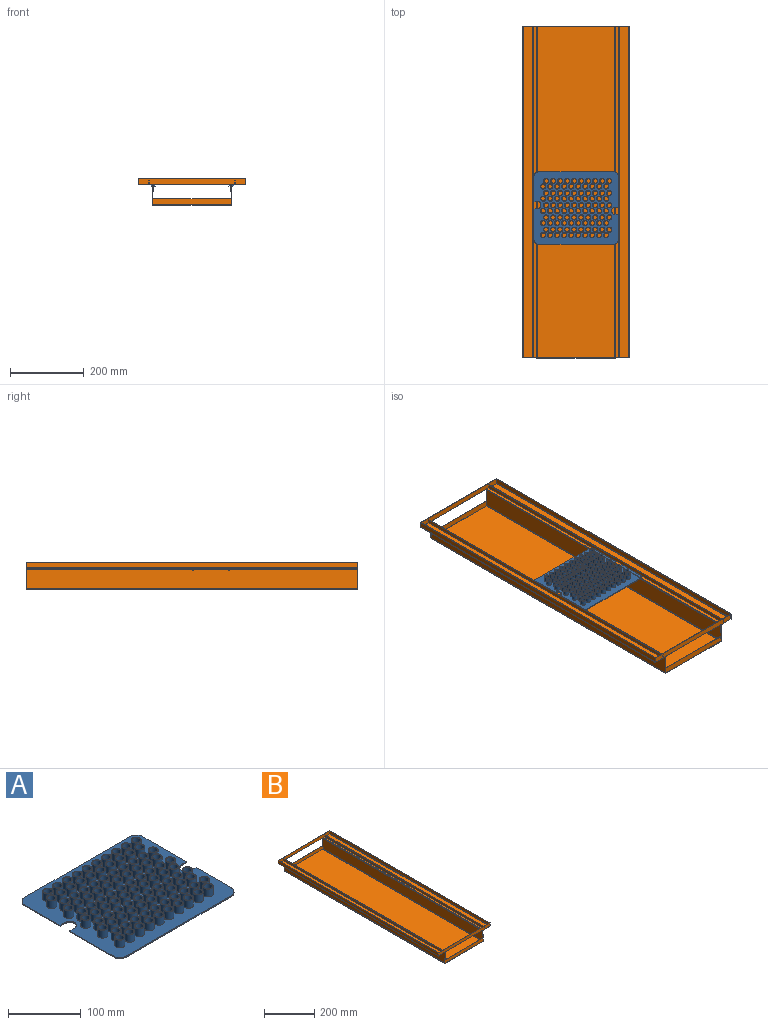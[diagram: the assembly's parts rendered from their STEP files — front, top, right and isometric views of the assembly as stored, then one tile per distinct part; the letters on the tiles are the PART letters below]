
ASSEMBLY  parts=2 mates=1
PART A: 338 faces, bbox 229x197x19 mm
  f0: plane 203x2mm, normal (0,1,0), area 406mm2, adj f1,f115,f116,f117
  f1: cylinder r=13mm len=13mm, axis (0,0,-1), area 37.4mm2, adj f0,f2,f116,f117,f136
  f2: plane 68x1mm, normal (-1,0,0), area 68mm2, adj f1,f3,f116,f136
  f3: plane 9.5x2mm, normal (0,-1,0), area 18.5mm2, adj f2,f4,f116,f117,f136
  f4: cylinder r=9.5mm len=19mm, axis (0,0,-1), area 59.7mm2, adj f3,f5,f116,f117
  f5: plane 9.5x2mm, normal (0,1,0), area 18.5mm2, adj f4,f6,f116,f117,f137
  f6: plane 84x1mm, normal (-1,0,0), area 84mm2, adj f5,f7,f116,f137
  f7: cylinder r=13mm len=13mm, axis (0,0,-1), area 37.4mm2, adj f6,f8,f116,f117,f137
  f8: plane 203x2mm, normal (0,-1,0), area 406mm2, adj f7,f9,f116,f117
  f9: cylinder r=13mm len=13mm, axis (0,0,-1), area 37.4mm2, adj f8,f10,f116,f117,f135
  f10: plane 68x1mm, normal (1,0,0), area 68mm2, adj f9,f11,f116,f135
  f11: plane 9.5x2mm, normal (0,1,0), area 18.5mm2, adj f10,f12,f116,f117,f135
  f12: cylinder r=9.5mm len=19mm, axis (0,0,-1), area 59.7mm2, adj f11,f13,f116,f117
  f13: plane 9.5x2mm, normal (0,-1,0), area 18.5mm2, adj f12,f14,f116,f117,f134
  f14: plane 84x1mm, normal (1,0,0), area 84mm2, adj f13,f115,f116,f134
  f15: cylinder r=6mm len=15mm, axis (0,0,-1), area 565.5mm2, adj f117,f229
  f16: cylinder r=6mm len=15mm, axis (0,0,-1), area 565.5mm2, adj f117,f337
  f17: cylinder r=6mm len=15mm, axis (0,0,-1), area 565.5mm2, adj f117,f231
  f18: cylinder r=6mm len=15mm, axis (0,0,-1), area 565.5mm2, adj f117,f233
  f19: cylinder r=6mm len=15mm, axis (0,0,-1), area 565.5mm2, adj f117,f235
  f20: cylinder r=6mm len=15mm, axis (0,0,-1), area 565.5mm2, adj f117,f237
  f21: cylinder r=6mm len=15mm, axis (0,0,-1), area 565.5mm2, adj f117,f219
  f22: cylinder r=6mm len=15mm, axis (0,0,-1), area 565.5mm2, adj f117,f221
  f23: cylinder r=6mm len=15mm, axis (0,0,-1), area 565.5mm2, adj f117,f223
  f24: cylinder r=6mm len=15mm, axis (0,0,-1), area 565.5mm2, adj f117,f225
  f25: cylinder r=6mm len=15mm, axis (0,0,-1), area 565.5mm2, adj f117,f227
  f26: cylinder r=6mm len=15mm, axis (0,0,-1), area 565.5mm2, adj f117,f209
  f27: cylinder r=6mm len=15mm, axis (0,0,-1), area 565.5mm2, adj f117,f211
  f28: cylinder r=6mm len=15mm, axis (0,0,-1), area 565.5mm2, adj f117,f213
  f29: cylinder r=6mm len=15mm, axis (0,0,-1), area 565.5mm2, adj f117,f215
  f30: cylinder r=6mm len=15mm, axis (0,0,-1), area 565.5mm2, adj f117,f217
  f31: cylinder r=6mm len=15mm, axis (0,0,-1), area 565.5mm2, adj f117,f199
  f32: cylinder r=6mm len=15mm, axis (0,0,-1), area 565.5mm2, adj f117,f201
  f33: cylinder r=6mm len=15mm, axis (0,0,-1), area 565.5mm2, adj f117,f203
  f34: cylinder r=6mm len=15mm, axis (0,0,-1), area 565.5mm2, adj f117,f205
  f35: cylinder r=6mm len=15mm, axis (0,0,-1), area 565.5mm2, adj f117,f207
  f36: cylinder r=6mm len=15mm, axis (0,0,-1), area 565.5mm2, adj f117,f189
  f37: cylinder r=6mm len=15mm, axis (0,0,-1), area 565.5mm2, adj f117,f191
  f38: cylinder r=6mm len=15mm, axis (0,0,-1), area 565.5mm2, adj f117,f193
  f39: cylinder r=6mm len=15mm, axis (0,0,-1), area 565.5mm2, adj f117,f195
  f40: cylinder r=6mm len=15mm, axis (0,0,-1), area 565.5mm2, adj f117,f197
  f41: cylinder r=6mm len=15mm, axis (0,0,-1), area 565.5mm2, adj f117,f179
  f42: cylinder r=6mm len=15mm, axis (0,0,-1), area 565.5mm2, adj f117,f181
  f43: cylinder r=6mm len=15mm, axis (0,0,-1), area 565.5mm2, adj f117,f183
  f44: cylinder r=6mm len=15mm, axis (0,0,-1), area 565.5mm2, adj f117,f185
  f45: cylinder r=6mm len=15mm, axis (0,0,-1), area 565.5mm2, adj f117,f187
  f46: cylinder r=6mm len=15mm, axis (0,0,-1), area 565.5mm2, adj f117,f169
  f47: cylinder r=6mm len=15mm, axis (0,0,-1), area 565.5mm2, adj f117,f171
  f48: cylinder r=6mm len=15mm, axis (0,0,-1), area 565.5mm2, adj f117,f173
  f49: cylinder r=6mm len=15mm, axis (0,0,-1), area 565.5mm2, adj f117,f175
  f50: cylinder r=6mm len=15mm, axis (0,0,-1), area 565.5mm2, adj f117,f177
  f51: cylinder r=6mm len=15mm, axis (0,0,-1), area 565.5mm2, adj f117,f159
  f52: cylinder r=6mm len=15mm, axis (0,0,-1), area 565.5mm2, adj f117,f161
  f53: cylinder r=6mm len=15mm, axis (0,0,-1), area 565.5mm2, adj f117,f163
  f54: cylinder r=6mm len=15mm, axis (0,0,-1), area 565.5mm2, adj f117,f165
  f55: cylinder r=6mm len=15mm, axis (0,0,-1), area 565.5mm2, adj f117,f167
  f56: cylinder r=6mm len=15mm, axis (0,0,-1), area 565.5mm2, adj f117,f149
  f57: cylinder r=6mm len=15mm, axis (0,0,-1), area 565.5mm2, adj f117,f151
  f58: cylinder r=6mm len=15mm, axis (0,0,-1), area 565.5mm2, adj f117,f153
  f59: cylinder r=6mm len=15mm, axis (0,0,-1), area 565.5mm2, adj f117,f155
  f60: cylinder r=6mm len=15mm, axis (0,0,-1), area 565.5mm2, adj f117,f157
  f61: cylinder r=6mm len=15mm, axis (0,0,-1), area 565.5mm2, adj f117,f139
  f62: cylinder r=6mm len=15mm, axis (0,0,-1), area 565.5mm2, adj f117,f141
  f63: cylinder r=6mm len=15mm, axis (0,0,-1), area 565.5mm2, adj f117,f143
  f64: cylinder r=6mm len=15mm, axis (0,0,-1), area 565.5mm2, adj f117,f145
  f65: cylinder r=6mm len=15mm, axis (0,0,-1), area 565.5mm2, adj f117,f147
  f66: cylinder r=6mm len=15mm, axis (0,0,-1), area 565.5mm2, adj f117,f335
  f67: cylinder r=6mm len=15mm, axis (0,0,-1), area 565.5mm2, adj f117,f333
  f68: cylinder r=6mm len=15mm, axis (0,0,-1), area 565.5mm2, adj f117,f331
  f69: cylinder r=6mm len=15mm, axis (0,0,-1), area 565.5mm2, adj f117,f329
  f70: cylinder r=6mm len=15mm, axis (0,0,-1), area 565.5mm2, adj f117,f327
  f71: cylinder r=6mm len=15mm, axis (0,0,-1), area 565.5mm2, adj f117,f325
  f72: cylinder r=6mm len=15mm, axis (0,0,-1), area 565.5mm2, adj f117,f323
  f73: cylinder r=6mm len=15mm, axis (0,0,-1), area 565.5mm2, adj f117,f321
  f74: cylinder r=6mm len=15mm, axis (0,0,-1), area 565.5mm2, adj f117,f319
  f75: cylinder r=6mm len=15mm, axis (0,0,-1), area 565.5mm2, adj f117,f317
  f76: cylinder r=6mm len=15mm, axis (0,0,-1), area 565.5mm2, adj f117,f315
  f77: cylinder r=6mm len=15mm, axis (0,0,-1), area 565.5mm2, adj f117,f313
  f78: cylinder r=6mm len=15mm, axis (0,0,-1), area 565.5mm2, adj f117,f311
  f79: cylinder r=6mm len=15mm, axis (0,0,-1), area 565.5mm2, adj f117,f309
  f80: cylinder r=6mm len=15mm, axis (0,0,-1), area 565.5mm2, adj f117,f307
  f81: cylinder r=6mm len=15mm, axis (0,0,-1), area 565.5mm2, adj f117,f305
  f82: cylinder r=6mm len=15mm, axis (0,0,-1), area 565.5mm2, adj f117,f303
  f83: cylinder r=6mm len=15mm, axis (0,0,-1), area 565.5mm2, adj f117,f301
  f84: cylinder r=6mm len=15mm, axis (0,0,-1), area 565.5mm2, adj f117,f299
  f85: cylinder r=6mm len=15mm, axis (0,0,-1), area 565.5mm2, adj f117,f297
  f86: cylinder r=6mm len=15mm, axis (0,0,-1), area 565.5mm2, adj f117,f295
  f87: cylinder r=6mm len=15mm, axis (0,0,-1), area 565.5mm2, adj f117,f293
  f88: cylinder r=6mm len=15mm, axis (0,0,-1), area 565.5mm2, adj f117,f291
  f89: cylinder r=6mm len=15mm, axis (0,0,-1), area 565.5mm2, adj f117,f289
  f90: cylinder r=6mm len=15mm, axis (0,0,-1), area 565.5mm2, adj f117,f287
  f91: cylinder r=6mm len=15mm, axis (0,0,-1), area 565.5mm2, adj f117,f285
  f92: cylinder r=6mm len=15mm, axis (0,0,-1), area 565.5mm2, adj f117,f283
  f93: cylinder r=6mm len=15mm, axis (0,0,-1), area 565.5mm2, adj f117,f281
  f94: cylinder r=6mm len=15mm, axis (0,0,-1), area 565.5mm2, adj f117,f279
  f95: cylinder r=6mm len=15mm, axis (0,0,-1), area 565.5mm2, adj f117,f277
  f96: cylinder r=6mm len=15mm, axis (0,0,-1), area 565.5mm2, adj f117,f275
  f97: cylinder r=6mm len=15mm, axis (0,0,-1), area 565.5mm2, adj f117,f273
  f98: cylinder r=6mm len=15mm, axis (0,0,-1), area 565.5mm2, adj f117,f271
  f99: cylinder r=6mm len=15mm, axis (0,0,-1), area 565.5mm2, adj f117,f269
  f100: cylinder r=6mm len=15mm, axis (0,0,-1), area 565.5mm2, adj f117,f267
  f101: cylinder r=6mm len=15mm, axis (0,0,-1), area 565.5mm2, adj f117,f265
  f102: cylinder r=6mm len=15mm, axis (0,0,-1), area 565.5mm2, adj f117,f263
  f103: cylinder r=6mm len=15mm, axis (0,0,-1), area 565.5mm2, adj f117,f261
  f104: cylinder r=6mm len=15mm, axis (0,0,-1), area 565.5mm2, adj f117,f259
  f105: cylinder r=6mm len=15mm, axis (0,0,-1), area 565.5mm2, adj f117,f257
  f106: cylinder r=6mm len=15mm, axis (0,0,-1), area 565.5mm2, adj f117,f255
  f107: cylinder r=6mm len=15mm, axis (0,0,-1), area 565.5mm2, adj f117,f253
  f108: cylinder r=6mm len=15mm, axis (0,0,-1), area 565.5mm2, adj f117,f251
  f109: cylinder r=6mm len=15mm, axis (0,0,-1), area 565.5mm2, adj f117,f249
  f110: cylinder r=6mm len=15mm, axis (0,0,-1), area 565.5mm2, adj f117,f247
  f111: cylinder r=6mm len=15mm, axis (0,0,-1), area 565.5mm2, adj f117,f245
  f112: cylinder r=6mm len=15mm, axis (0,0,-1), area 565.5mm2, adj f117,f243
  f113: cylinder r=6mm len=15mm, axis (0,0,-1), area 565.5mm2, adj f117,f241
  f114: cylinder r=6mm len=15mm, axis (0,0,-1), area 565.5mm2, adj f117,f239
  f115: cylinder r=13mm len=13mm, axis (0,0,-1), area 37.4mm2, adj f0,f14,f116,f117,f134
  f116: plane 229x197mm, normal (0,0,1), area 28929.6mm2, adj f0,f1,f2,f3,f4,f5,f6,f7
  f117: plane 227x197mm, normal (0,0,-1), area 32640.2mm2, adj f0,f1,f3,f4,f5,f7,f8,f9
  f118: plane 14x4mm, normal (0,-1,0), area 48mm2, adj f117,f120,f121,f137
  f119: plane 14x4mm, normal (0,1,0), area 48mm2, adj f117,f120,f121,f137
  f120: plane 4x1mm, normal (1,0,0), area 4mm2, adj f117,f118,f119,f121
  f121: plane 10x1mm, normal (0,0,-1), area 10mm2, adj f118,f119,f120,f137
  f122: plane 14x4mm, normal (0,-1,0), area 48mm2, adj f117,f124,f125,f136
  f123: plane 14x4mm, normal (0,1,0), area 48mm2, adj f117,f124,f125,f136
  f124: plane 4x1mm, normal (1,0,0), area 4mm2, adj f117,f122,f123,f125
  f125: plane 10x1mm, normal (0,0,-1), area 10mm2, adj f122,f123,f124,f136
  f126: plane 14x4mm, normal (0,-1,0), area 48mm2, adj f117,f127,f129,f134
  f127: plane 4x1mm, normal (-1,0,0), area 4mm2, adj f117,f126,f128,f129
  f128: plane 14x4mm, normal (0,1,0), area 48mm2, adj f117,f127,f129,f134
  f129: plane 10x1mm, normal (0,0,-1), area 10mm2, adj f126,f127,f128,f134
  f130: plane 14x4mm, normal (0,-1,0), area 48mm2, adj f117,f131,f133,f135
  f131: plane 4x1mm, normal (-1,0,0), area 4mm2, adj f117,f130,f132,f133
  f132: plane 14x4mm, normal (0,1,0), area 48mm2, adj f117,f131,f133,f135
  f133: plane 10x1mm, normal (0,0,-1), area 10mm2, adj f130,f131,f132,f135
  f134: plane 89x5mm, normal (0.71,0,-0.71), area 129.2mm2, adj f13,f14,f115,f117,f126,f128,f129
  f135: plane 73x5mm, normal (0.71,0,-0.71), area 106.6mm2, adj f9,f10,f11,f117,f130,f132,f133
  f136: plane 73x5mm, normal (-0.71,0,-0.71), area 106.6mm2, adj f1,f2,f3,f117,f122,f123,f125
  f137: plane 89x5mm, normal (-0.71,0,-0.71), area 129.2mm2, adj f5,f6,f7,f117,f118,f119,f121
  f138: cylinder r=7mm len=14mm, axis (0,0,-1), area 571.8mm2, adj f116,f139
  f139: plane 14x14mm, normal (0,0,1), area 40.8mm2, adj f61,f138
  f140: cylinder r=7mm len=14mm, axis (0,0,-1), area 571.8mm2, adj f116,f141
  f141: plane 14x14mm, normal (0,0,1), area 40.8mm2, adj f62,f140
  f142: cylinder r=7mm len=14mm, axis (0,0,-1), area 571.8mm2, adj f116,f143
  f143: plane 14x14mm, normal (0,0,1), area 40.8mm2, adj f63,f142
  f144: cylinder r=7mm len=14mm, axis (0,0,-1), area 571.8mm2, adj f116,f145
  f145: plane 14x14mm, normal (0,0,1), area 40.8mm2, adj f64,f144
  f146: cylinder r=7mm len=14mm, axis (0,0,-1), area 571.8mm2, adj f116,f147
  f147: plane 14x14mm, normal (0,0,1), area 40.8mm2, adj f65,f146
  f148: cylinder r=7mm len=14mm, axis (0,0,-1), area 571.8mm2, adj f116,f149
  f149: plane 14x14mm, normal (0,0,1), area 40.8mm2, adj f56,f148
  f150: cylinder r=7mm len=14mm, axis (0,0,-1), area 571.8mm2, adj f116,f151
  f151: plane 14x14mm, normal (0,0,1), area 40.8mm2, adj f57,f150
  f152: cylinder r=7mm len=14mm, axis (0,0,-1), area 571.8mm2, adj f116,f153
  f153: plane 14x14mm, normal (0,0,1), area 40.8mm2, adj f58,f152
  f154: cylinder r=7mm len=14mm, axis (0,0,-1), area 571.8mm2, adj f116,f155
  f155: plane 14x14mm, normal (0,0,1), area 40.8mm2, adj f59,f154
  f156: cylinder r=7mm len=14mm, axis (0,0,-1), area 571.8mm2, adj f116,f157
  f157: plane 14x14mm, normal (0,0,1), area 40.8mm2, adj f60,f156
  f158: cylinder r=7mm len=14mm, axis (0,0,-1), area 571.8mm2, adj f116,f159
  f159: plane 14x14mm, normal (0,0,1), area 40.8mm2, adj f51,f158
  f160: cylinder r=7mm len=14mm, axis (0,0,-1), area 571.8mm2, adj f116,f161
  f161: plane 14x14mm, normal (0,0,1), area 40.8mm2, adj f52,f160
  f162: cylinder r=7mm len=14mm, axis (0,0,-1), area 571.8mm2, adj f116,f163
  f163: plane 14x14mm, normal (0,0,1), area 40.8mm2, adj f53,f162
  f164: cylinder r=7mm len=14mm, axis (0,0,-1), area 571.8mm2, adj f116,f165
  f165: plane 14x14mm, normal (0,0,1), area 40.8mm2, adj f54,f164
  f166: cylinder r=7mm len=14mm, axis (0,0,-1), area 571.8mm2, adj f116,f167
  f167: plane 14x14mm, normal (0,0,1), area 40.8mm2, adj f55,f166
  f168: cylinder r=7mm len=14mm, axis (0,0,-1), area 571.8mm2, adj f116,f169
  f169: plane 14x14mm, normal (0,0,1), area 40.8mm2, adj f46,f168
  f170: cylinder r=7mm len=14mm, axis (0,0,-1), area 571.8mm2, adj f116,f171
  f171: plane 14x14mm, normal (0,0,1), area 40.8mm2, adj f47,f170
  f172: cylinder r=7mm len=14mm, axis (0,0,-1), area 571.8mm2, adj f116,f173
  f173: plane 14x14mm, normal (0,0,1), area 40.8mm2, adj f48,f172
  f174: cylinder r=7mm len=14mm, axis (0,0,-1), area 571.8mm2, adj f116,f175
  f175: plane 14x14mm, normal (0,0,1), area 40.8mm2, adj f49,f174
  f176: cylinder r=7mm len=14mm, axis (0,0,-1), area 571.8mm2, adj f116,f177
  f177: plane 14x14mm, normal (0,0,1), area 40.8mm2, adj f50,f176
  f178: cylinder r=7mm len=14mm, axis (0,0,-1), area 571.8mm2, adj f116,f179
  f179: plane 14x14mm, normal (0,0,1), area 40.8mm2, adj f41,f178
  f180: cylinder r=7mm len=14mm, axis (0,0,-1), area 571.8mm2, adj f116,f181
  f181: plane 14x14mm, normal (0,0,1), area 40.8mm2, adj f42,f180
  f182: cylinder r=7mm len=14mm, axis (0,0,-1), area 571.8mm2, adj f116,f183
  f183: plane 14x14mm, normal (0,0,1), area 40.8mm2, adj f43,f182
  f184: cylinder r=7mm len=14mm, axis (0,0,-1), area 571.8mm2, adj f116,f185
  f185: plane 14x14mm, normal (0,0,1), area 40.8mm2, adj f44,f184
  f186: cylinder r=7mm len=14mm, axis (0,0,-1), area 571.8mm2, adj f116,f187
  f187: plane 14x14mm, normal (0,0,1), area 40.8mm2, adj f45,f186
  f188: cylinder r=7mm len=14mm, axis (0,0,-1), area 571.8mm2, adj f116,f189
  f189: plane 14x14mm, normal (0,0,1), area 40.8mm2, adj f36,f188
  f190: cylinder r=7mm len=14mm, axis (0,0,-1), area 571.8mm2, adj f116,f191
  f191: plane 14x14mm, normal (0,0,1), area 40.8mm2, adj f37,f190
  f192: cylinder r=7mm len=14mm, axis (0,0,-1), area 571.8mm2, adj f116,f193
  f193: plane 14x14mm, normal (0,0,1), area 40.8mm2, adj f38,f192
  f194: cylinder r=7mm len=14mm, axis (0,0,-1), area 571.8mm2, adj f116,f195
  f195: plane 14x14mm, normal (0,0,1), area 40.8mm2, adj f39,f194
  f196: cylinder r=7mm len=14mm, axis (0,0,-1), area 571.8mm2, adj f116,f197
  f197: plane 14x14mm, normal (0,0,1), area 40.8mm2, adj f40,f196
  f198: cylinder r=7mm len=14mm, axis (0,0,-1), area 571.8mm2, adj f116,f199
  f199: plane 14x14mm, normal (0,0,1), area 40.8mm2, adj f31,f198
  f200: cylinder r=7mm len=14mm, axis (0,0,-1), area 571.8mm2, adj f116,f201
  f201: plane 14x14mm, normal (0,0,1), area 40.8mm2, adj f32,f200
  f202: cylinder r=7mm len=14mm, axis (0,0,-1), area 571.8mm2, adj f116,f203
  f203: plane 14x14mm, normal (0,0,1), area 40.8mm2, adj f33,f202
  f204: cylinder r=7mm len=14mm, axis (0,0,-1), area 571.8mm2, adj f116,f205
  f205: plane 14x14mm, normal (0,0,1), area 40.8mm2, adj f34,f204
  f206: cylinder r=7mm len=14mm, axis (0,0,-1), area 571.8mm2, adj f116,f207
  f207: plane 14x14mm, normal (0,0,1), area 40.8mm2, adj f35,f206
  f208: cylinder r=7mm len=14mm, axis (0,0,-1), area 571.8mm2, adj f116,f209
  f209: plane 14x14mm, normal (0,0,1), area 40.8mm2, adj f26,f208
  f210: cylinder r=7mm len=14mm, axis (0,0,-1), area 571.8mm2, adj f116,f211
  f211: plane 14x14mm, normal (0,0,1), area 40.8mm2, adj f27,f210
  f212: cylinder r=7mm len=14mm, axis (0,0,-1), area 571.8mm2, adj f116,f213
  f213: plane 14x14mm, normal (0,0,1), area 40.8mm2, adj f28,f212
  f214: cylinder r=7mm len=14mm, axis (0,0,-1), area 571.8mm2, adj f116,f215
  f215: plane 14x14mm, normal (0,0,1), area 40.8mm2, adj f29,f214
  f216: cylinder r=7mm len=14mm, axis (0,0,-1), area 571.8mm2, adj f116,f217
  f217: plane 14x14mm, normal (0,0,1), area 40.8mm2, adj f30,f216
  f218: cylinder r=7mm len=14mm, axis (0,0,-1), area 571.8mm2, adj f116,f219
  f219: plane 14x14mm, normal (0,0,1), area 40.8mm2, adj f21,f218
  f220: cylinder r=7mm len=14mm, axis (0,0,-1), area 571.8mm2, adj f116,f221
  f221: plane 14x14mm, normal (0,0,1), area 40.8mm2, adj f22,f220
  f222: cylinder r=7mm len=14mm, axis (0,0,-1), area 571.8mm2, adj f116,f223
  f223: plane 14x14mm, normal (0,0,1), area 40.8mm2, adj f23,f222
  f224: cylinder r=7mm len=14mm, axis (0,0,-1), area 571.8mm2, adj f116,f225
  f225: plane 14x14mm, normal (0,0,1), area 40.8mm2, adj f24,f224
  f226: cylinder r=7mm len=14mm, axis (0,0,-1), area 571.8mm2, adj f116,f227
  f227: plane 14x14mm, normal (0,0,1), area 40.8mm2, adj f25,f226
  f228: cylinder r=7mm len=14mm, axis (0,0,-1), area 571.8mm2, adj f116,f229
  f229: plane 14x14mm, normal (0,0,1), area 40.8mm2, adj f15,f228
  f230: cylinder r=7mm len=14mm, axis (0,0,-1), area 571.8mm2, adj f116,f231
  f231: plane 14x14mm, normal (0,0,1), area 40.8mm2, adj f17,f230
  f232: cylinder r=7mm len=14mm, axis (0,0,-1), area 571.8mm2, adj f116,f233
  f233: plane 14x14mm, normal (0,0,1), area 40.8mm2, adj f18,f232
  f234: cylinder r=7mm len=14mm, axis (0,0,-1), area 571.8mm2, adj f116,f235
  f235: plane 14x14mm, normal (0,0,1), area 40.8mm2, adj f19,f234
  f236: cylinder r=7mm len=14mm, axis (0,0,-1), area 571.8mm2, adj f116,f237
  f237: plane 14x14mm, normal (0,0,1), area 40.8mm2, adj f20,f236
  f238: cylinder r=7mm len=14mm, axis (0,0,-1), area 571.8mm2, adj f116,f239
  f239: plane 14x14mm, normal (0,0,1), area 40.8mm2, adj f114,f238
  f240: cylinder r=7mm len=14mm, axis (0,0,-1), area 571.8mm2, adj f116,f241
  f241: plane 14x14mm, normal (0,0,1), area 40.8mm2, adj f113,f240
  f242: cylinder r=7mm len=14mm, axis (0,0,-1), area 571.8mm2, adj f116,f243
  f243: plane 14x14mm, normal (0,0,1), area 40.8mm2, adj f112,f242
  f244: cylinder r=7mm len=14mm, axis (0,0,-1), area 571.8mm2, adj f116,f245
  f245: plane 14x14mm, normal (0,0,1), area 40.8mm2, adj f111,f244
  f246: cylinder r=7mm len=14mm, axis (0,0,-1), area 571.8mm2, adj f116,f247
  f247: plane 14x14mm, normal (0,0,1), area 40.8mm2, adj f110,f246
  f248: cylinder r=7mm len=14mm, axis (0,0,-1), area 571.8mm2, adj f116,f249
  f249: plane 14x14mm, normal (0,0,1), area 40.8mm2, adj f109,f248
  f250: cylinder r=7mm len=14mm, axis (0,0,-1), area 571.8mm2, adj f116,f251
  f251: plane 14x14mm, normal (0,0,1), area 40.8mm2, adj f108,f250
  f252: cylinder r=7mm len=14mm, axis (0,0,-1), area 571.8mm2, adj f116,f253
  f253: plane 14x14mm, normal (0,0,1), area 40.8mm2, adj f107,f252
  f254: cylinder r=7mm len=14mm, axis (0,0,-1), area 571.8mm2, adj f116,f255
  f255: plane 14x14mm, normal (0,0,1), area 40.8mm2, adj f106,f254
  f256: cylinder r=7mm len=14mm, axis (0,0,-1), area 571.8mm2, adj f116,f257
  f257: plane 14x14mm, normal (0,0,1), area 40.8mm2, adj f105,f256
  f258: cylinder r=7mm len=14mm, axis (0,0,-1), area 571.8mm2, adj f116,f259
  f259: plane 14x14mm, normal (0,0,1), area 40.8mm2, adj f104,f258
  f260: cylinder r=7mm len=14mm, axis (0,0,-1), area 571.8mm2, adj f116,f261
  f261: plane 14x14mm, normal (0,0,1), area 40.8mm2, adj f103,f260
  f262: cylinder r=7mm len=14mm, axis (0,0,-1), area 571.8mm2, adj f116,f263
  f263: plane 14x14mm, normal (0,0,1), area 40.8mm2, adj f102,f262
  f264: cylinder r=7mm len=14mm, axis (0,0,-1), area 571.8mm2, adj f116,f265
  f265: plane 14x14mm, normal (0,0,1), area 40.8mm2, adj f101,f264
  f266: cylinder r=7mm len=14mm, axis (0,0,-1), area 571.8mm2, adj f116,f267
  f267: plane 14x14mm, normal (0,0,1), area 40.8mm2, adj f100,f266
  f268: cylinder r=7mm len=14mm, axis (0,0,-1), area 571.8mm2, adj f116,f269
  f269: plane 14x14mm, normal (0,0,1), area 40.8mm2, adj f99,f268
  f270: cylinder r=7mm len=14mm, axis (0,0,-1), area 571.8mm2, adj f116,f271
  f271: plane 14x14mm, normal (0,0,1), area 40.8mm2, adj f98,f270
  f272: cylinder r=7mm len=14mm, axis (0,0,-1), area 571.8mm2, adj f116,f273
  f273: plane 14x14mm, normal (0,0,1), area 40.8mm2, adj f97,f272
  f274: cylinder r=7mm len=14mm, axis (0,0,-1), area 571.8mm2, adj f116,f275
  f275: plane 14x14mm, normal (0,0,1), area 40.8mm2, adj f96,f274
  f276: cylinder r=7mm len=14mm, axis (0,0,-1), area 571.8mm2, adj f116,f277
  f277: plane 14x14mm, normal (0,0,1), area 40.8mm2, adj f95,f276
  f278: cylinder r=7mm len=14mm, axis (0,0,-1), area 571.8mm2, adj f116,f279
  f279: plane 14x14mm, normal (0,0,1), area 40.8mm2, adj f94,f278
  f280: cylinder r=7mm len=14mm, axis (0,0,-1), area 571.8mm2, adj f116,f281
  f281: plane 14x14mm, normal (0,0,1), area 40.8mm2, adj f93,f280
  f282: cylinder r=7mm len=14mm, axis (0,0,-1), area 571.8mm2, adj f116,f283
  f283: plane 14x14mm, normal (0,0,1), area 40.8mm2, adj f92,f282
  f284: cylinder r=7mm len=14mm, axis (0,0,-1), area 571.8mm2, adj f116,f285
  f285: plane 14x14mm, normal (0,0,1), area 40.8mm2, adj f91,f284
  f286: cylinder r=7mm len=14mm, axis (0,0,-1), area 571.8mm2, adj f116,f287
  f287: plane 14x14mm, normal (0,0,1), area 40.8mm2, adj f90,f286
  f288: cylinder r=7mm len=14mm, axis (0,0,-1), area 571.8mm2, adj f116,f289
  f289: plane 14x14mm, normal (0,0,1), area 40.8mm2, adj f89,f288
  f290: cylinder r=7mm len=14mm, axis (0,0,-1), area 571.8mm2, adj f116,f291
  f291: plane 14x14mm, normal (0,0,1), area 40.8mm2, adj f88,f290
  f292: cylinder r=7mm len=14mm, axis (0,0,-1), area 571.8mm2, adj f116,f293
  f293: plane 14x14mm, normal (0,0,1), area 40.8mm2, adj f87,f292
  f294: cylinder r=7mm len=14mm, axis (0,0,-1), area 571.8mm2, adj f116,f295
  f295: plane 14x14mm, normal (0,0,1), area 40.8mm2, adj f86,f294
  f296: cylinder r=7mm len=14mm, axis (0,0,-1), area 571.8mm2, adj f116,f297
  f297: plane 14x14mm, normal (0,0,1), area 40.8mm2, adj f85,f296
  f298: cylinder r=7mm len=14mm, axis (0,0,-1), area 571.8mm2, adj f116,f299
  f299: plane 14x14mm, normal (0,0,1), area 40.8mm2, adj f84,f298
  f300: cylinder r=7mm len=14mm, axis (0,0,-1), area 571.8mm2, adj f116,f301
  f301: plane 14x14mm, normal (0,0,1), area 40.8mm2, adj f83,f300
  f302: cylinder r=7mm len=14mm, axis (0,0,-1), area 571.8mm2, adj f116,f303
  f303: plane 14x14mm, normal (0,0,1), area 40.8mm2, adj f82,f302
  f304: cylinder r=7mm len=14mm, axis (0,0,-1), area 571.8mm2, adj f116,f305
  f305: plane 14x14mm, normal (0,0,1), area 40.8mm2, adj f81,f304
  f306: cylinder r=7mm len=14mm, axis (0,0,-1), area 571.8mm2, adj f116,f307
  f307: plane 14x14mm, normal (0,0,1), area 40.8mm2, adj f80,f306
  f308: cylinder r=7mm len=14mm, axis (0,0,-1), area 571.8mm2, adj f116,f309
  f309: plane 14x14mm, normal (0,0,1), area 40.8mm2, adj f79,f308
  f310: cylinder r=7mm len=14mm, axis (0,0,-1), area 571.8mm2, adj f116,f311
  f311: plane 14x14mm, normal (0,0,1), area 40.8mm2, adj f78,f310
  f312: cylinder r=7mm len=14mm, axis (0,0,-1), area 571.8mm2, adj f116,f313
  f313: plane 14x14mm, normal (0,0,1), area 40.8mm2, adj f77,f312
  f314: cylinder r=7mm len=14mm, axis (0,0,-1), area 571.8mm2, adj f116,f315
  f315: plane 14x14mm, normal (0,0,1), area 40.8mm2, adj f76,f314
  f316: cylinder r=7mm len=14mm, axis (0,0,-1), area 571.8mm2, adj f116,f317
  f317: plane 14x14mm, normal (0,0,1), area 40.8mm2, adj f75,f316
  f318: cylinder r=7mm len=14mm, axis (0,0,-1), area 571.8mm2, adj f116,f319
  f319: plane 14x14mm, normal (0,0,1), area 40.8mm2, adj f74,f318
  f320: cylinder r=7mm len=14mm, axis (0,0,-1), area 571.8mm2, adj f116,f321
  f321: plane 14x14mm, normal (0,0,1), area 40.8mm2, adj f73,f320
  f322: cylinder r=7mm len=14mm, axis (0,0,-1), area 571.8mm2, adj f116,f323
  f323: plane 14x14mm, normal (0,0,1), area 40.8mm2, adj f72,f322
  f324: cylinder r=7mm len=14mm, axis (0,0,-1), area 571.8mm2, adj f116,f325
  f325: plane 14x14mm, normal (0,0,1), area 40.8mm2, adj f71,f324
  f326: cylinder r=7mm len=14mm, axis (0,0,-1), area 571.8mm2, adj f116,f327
  f327: plane 14x14mm, normal (0,0,1), area 40.8mm2, adj f70,f326
  f328: cylinder r=7mm len=14mm, axis (0,0,-1), area 571.8mm2, adj f116,f329
  f329: plane 14x14mm, normal (0,0,1), area 40.8mm2, adj f69,f328
  f330: cylinder r=7mm len=14mm, axis (0,0,-1), area 571.8mm2, adj f116,f331
  f331: plane 14x14mm, normal (0,0,1), area 40.8mm2, adj f68,f330
  f332: cylinder r=7mm len=14mm, axis (0,0,-1), area 571.8mm2, adj f116,f333
  f333: plane 14x14mm, normal (0,0,1), area 40.8mm2, adj f67,f332
  f334: cylinder r=7mm len=14mm, axis (0,0,-1), area 571.8mm2, adj f116,f335
  f335: plane 14x14mm, normal (0,0,1), area 40.8mm2, adj f66,f334
  f336: cylinder r=7mm len=14mm, axis (0,0,-1), area 571.8mm2, adj f116,f337
  f337: plane 14x14mm, normal (0,0,1), area 40.8mm2, adj f16,f336
PART B: 49 faces, bbox 292x900x71 mm
  f0: plane 900x51.9mm, normal (1,0,-0.03), area 46705.3mm2, adj f3,f31,f32,f38,f43,f44,f47,f48
  f1: plane 898x210.73mm, normal (0,0,1), area 189239.8mm2, adj f2,f3,f44,f48
  f2: cylinder r=1.5mm len=898mm, axis (0,1,0), area 2162.9mm2, adj f1,f26,f44,f48
  f3: cylinder r=1.5mm len=898mm, axis (0,-1,0), area 2162.9mm2, adj f0,f1,f44,f48
  f4: plane 898x8.45mm, normal (0,0,1), area 7585.1mm2, adj f16,f37,f41,f45
  f5: plane 898x26.5mm, normal (0,0,1), area 23797mm2, adj f8,f17,f41,f45
  f6: plane 898x13.5mm, normal (-1,0,0), area 12123mm2, adj f8,f28,f41,f45
  f7: plane 898x13.5mm, normal (1,0,0), area 12123mm2, adj f9,f28,f41,f45
  f8: cylinder r=1.5mm len=898mm, axis (0,1,0), area 2115.9mm2, adj f5,f6,f41,f45
  f9: cylinder r=1.5mm len=898mm, axis (0,1,0), area 2115.9mm2, adj f7,f20,f41,f45
  f10: plane 898x9.5mm, normal (-1,0,0), area 8531mm2, adj f14,f20,f41,f45
  f11: plane 898x9.5mm, normal (1,0,0), area 8531mm2, adj f12,f27,f41,f45
  f12: cylinder r=0.5mm len=898mm, axis (0,-1,0), area 705.3mm2, adj f11,f13,f41,f45
  f13: plane 898x1mm, normal (0,0,1), area 898mm2, adj f12,f14,f41,f45
  f14: cylinder r=0.5mm len=898mm, axis (0,-1,0), area 705.3mm2, adj f10,f13,f41,f45
  f15: cylinder r=0.5mm len=898mm, axis (0,-1,0), area 705.3mm2, adj f16,f19,f41,f45
  f16: plane 898x9.5mm, normal (-1,0,0), area 8531mm2, adj f4,f15,f41,f45
  f17: plane 898x9.5mm, normal (1,0,0), area 8531mm2, adj f5,f18,f41,f45
  f18: cylinder r=0.5mm len=898mm, axis (0,-1,0), area 705.3mm2, adj f17,f19,f41,f45
  f19: plane 898x1mm, normal (0,0,1), area 898mm2, adj f15,f18,f41,f45
  f20: plane 898x26.5mm, normal (0,0,1), area 23797mm2, adj f9,f10,f41,f45
  f21: plane 900x51.9mm, normal (-1,0,0.03), area 46734.2mm2, adj f31,f32,f33,f40
  f22: plane 900x212.81mm, normal (0,0,-1), area 191525.2mm2, adj f31,f32,f33,f34
  f23: plane 900x51.9mm, normal (1,0,0.03), area 46734.2mm2, adj f31,f32,f34,f35
  f24: plane 900x36.91mm, normal (0,0,-1), area 33220.1mm2, adj f31,f32,f35,f36
  f25: plane 900x14.5mm, normal (1,0,0), area 13050mm2, adj f28,f31,f32,f36
  f26: plane 900x51.9mm, normal (-1,0,-0.03), area 46705.3mm2, adj f2,f31,f32,f37,f43,f44,f47,f48
  f27: plane 898x8.45mm, normal (0,0,1), area 7585.1mm2, adj f11,f38,f41,f45
  f28: plane 900x292mm, normal (0,0,1), area 2380mm2, adj f6,f7,f25,f29,f31,f32,f41,f45
  f29: plane 900x14.5mm, normal (-1,0,0), area 13050mm2, adj f28,f31,f32,f39
  f30: plane 900x36.91mm, normal (0,0,-1), area 33220.1mm2, adj f31,f32,f39,f40
  f31: plane 292x71mm, normal (0,1,0), area 8196.4mm2, adj f0,f21,f22,f23,f24,f25,f26,f28
  f32: plane 292x71mm, normal (0,-1,0), area 8196.4mm2, adj f0,f21,f22,f23,f24,f25,f26,f28
  f33: cylinder r=1.5mm len=900mm, axis (0,-1,0), area 2167.7mm2, adj f21,f22,f31,f32
  f34: cylinder r=1.5mm len=900mm, axis (0,1,0), area 2167.7mm2, adj f22,f23,f31,f32
  f35: cylinder r=1.5mm len=900mm, axis (0,1,0), area 2167.7mm2, adj f23,f24,f31,f32
  f36: cylinder r=1.5mm len=900mm, axis (0,-1,0), area 2120.6mm2, adj f24,f25,f31,f32
  f37: cylinder r=1.5mm len=900mm, axis (0,-1,0), area 2167.7mm2, adj f4,f26,f31,f32,f42,f46
  f38: cylinder r=1.5mm len=900mm, axis (0,-1,0), area 2167.7mm2, adj f0,f27,f31,f32,f42,f46
  f39: cylinder r=1.5mm len=900mm, axis (0,-1,0), area 2120.6mm2, adj f29,f30,f31,f32
  f40: cylinder r=1.5mm len=900mm, axis (0,1,0), area 2167.7mm2, adj f21,f30,f31,f32
  f41: plane 290x15mm, normal (0,1,0), area 4309.2mm2, adj f4,f5,f6,f7,f8,f9,f10,f11
  f42: plane 213.11x1mm, normal (0,0,-1), area 213.1mm2, adj f32,f37,f38,f41
  f43: plane 212.72x1mm, normal (0,0,1), area 212.7mm2, adj f0,f26,f32,f44
  f44: plane 213.73x16mm, normal (0,1,0), area 3411.5mm2, adj f0,f1,f2,f3,f26,f43
  f45: plane 290x15mm, normal (0,-1,0), area 4309.2mm2, adj f4,f5,f6,f7,f8,f9,f10,f11
  f46: plane 213.11x1mm, normal (0,0,-1), area 213.1mm2, adj f31,f37,f38,f45
  f47: plane 212.72x1mm, normal (0,0,1), area 212.7mm2, adj f0,f26,f31,f48
  f48: plane 213.73x16mm, normal (0,-1,0), area 3411.5mm2, adj f0,f1,f2,f3,f26,f47
PLACE A t=(136.17,161.07,208.37)mm
PLACE B t=(135.67,-245.43,184.87)mm fixed
MATE planar A.f14 <-> B.f16  axis (1,0,0) through (250.67,204.57,209.87)mm
